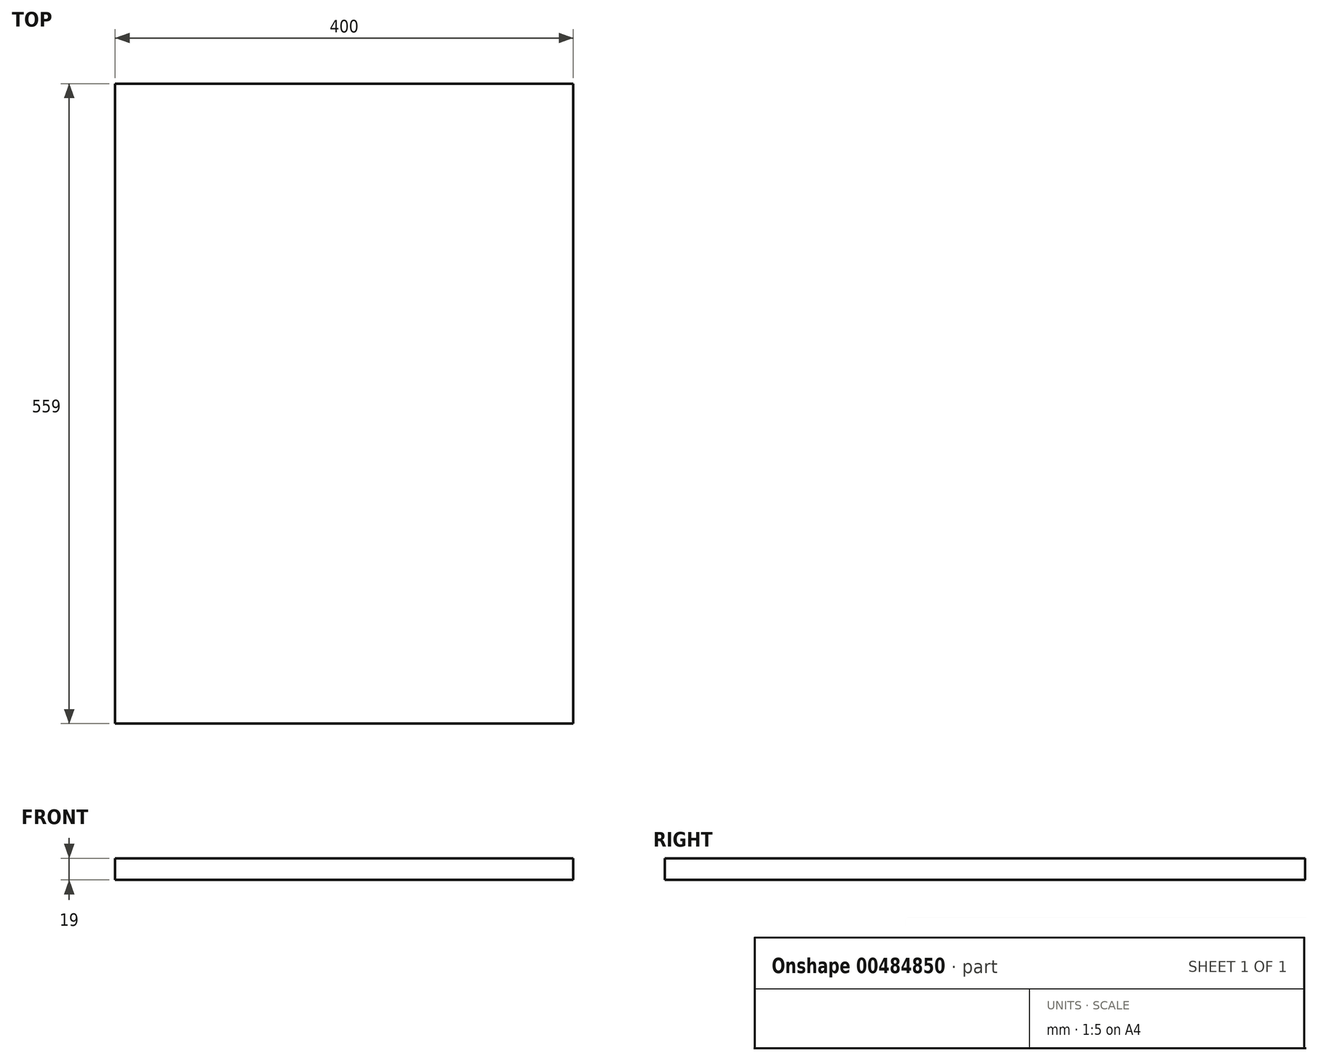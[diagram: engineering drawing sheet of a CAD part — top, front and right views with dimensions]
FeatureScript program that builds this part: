
annotation { "Feature Type Name" : "Feature", "Feature Type Description" : "" }
export const myFeature = defineFeature(function(context is Context, id is Id, definition is map)
    precondition{}
    {
        {
            var Q0;
            Q0=qCreatedBy(makeId("Top.planeOp"),FACE);
            var sketch = newSketch(context, id + "F0", { "sketchPlane" : qUnion([Q0])});
            skLineSegment(sketch, "E0.bottom", {"start": v(-181, 507.51) * mm, "end": v(219, 507.51) * mm});
            skLineSegment(sketch, "E0.top", {"start": v(-181, -51.49) * mm, "end": v(219, -51.49) * mm});
            skLineSegment(sketch, "E0.left", {"start": v(-181, 507.51) * mm, "end": v(-181, -51.49) * mm});
            skLineSegment(sketch, "E0.right", {"start": v(219, 507.51) * mm, "end": v(219, -51.49) * mm});
            skSolve(sketch);
        }
        {
            var Q0;
            Q0 = qSketchRegion(id + "F0", true);
            extrude(context, id + "F1", {"entities" : qUnion([Q0]), "depth" : 19 * mm});
        }
    });
